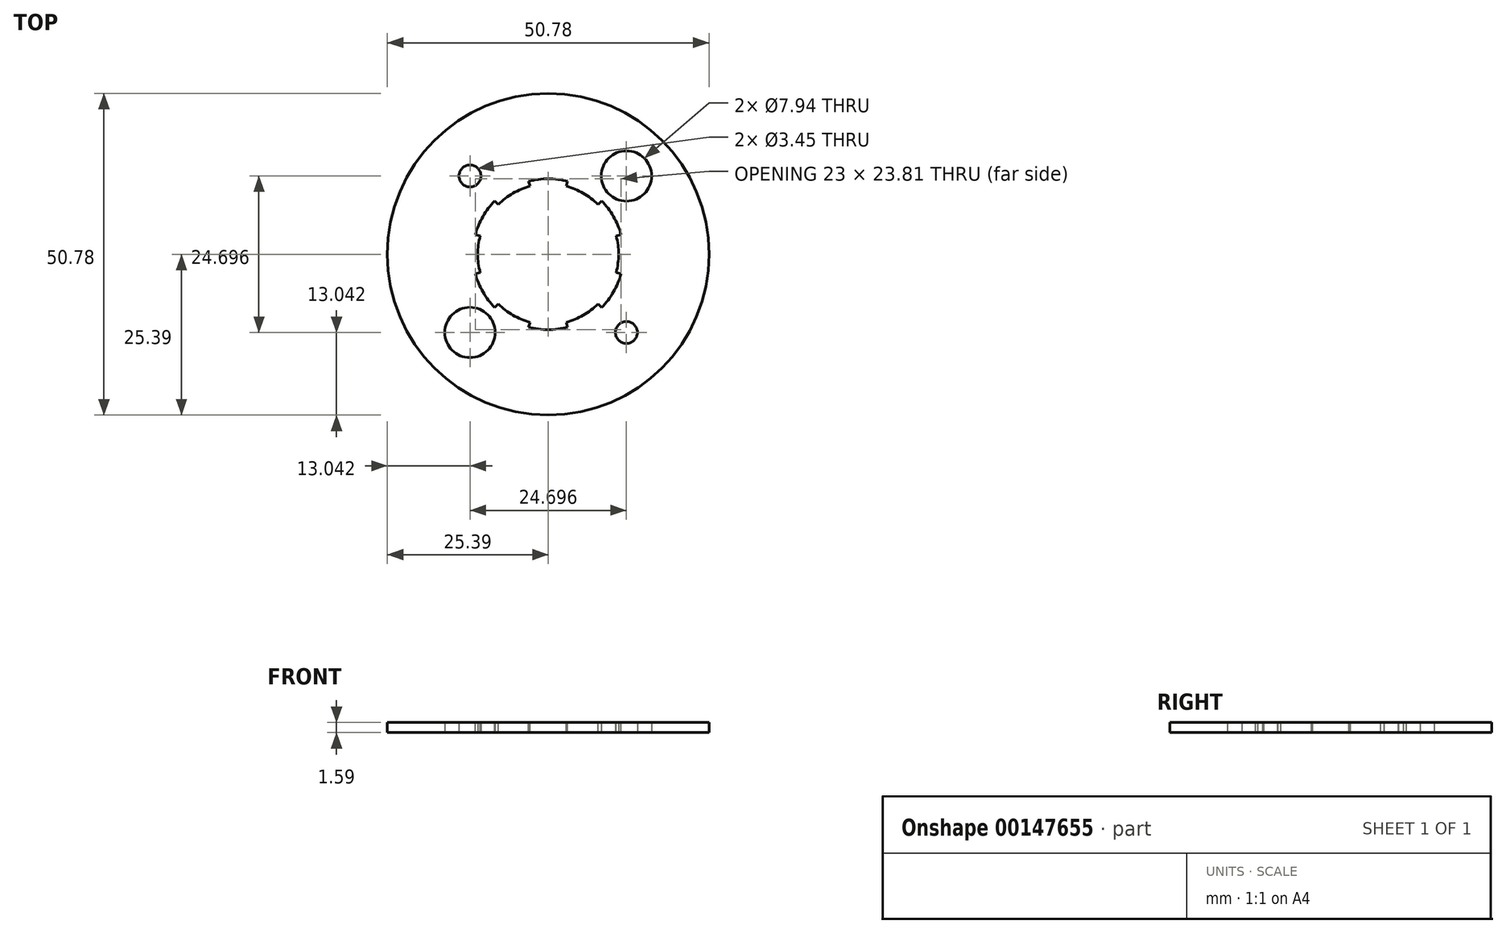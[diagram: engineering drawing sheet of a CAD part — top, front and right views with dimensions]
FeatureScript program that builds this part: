
annotation { "Feature Type Name" : "Feature", "Feature Type Description" : "" }
export const myFeature = defineFeature(function(context is Context, id is Id, definition is map)
    precondition{}
    {
        {
            var Q0;
            Q0=qCreatedBy(makeId("Top.planeOp"),FACE);
            var sketch = newSketch(context, id + "F0", { "sketchPlane" : qUnion([Q0])});
            skCircle(sketch, "E0", {"center": v(0, 0) * mm, "radius": 25.4 * mm});
            skCircle(sketch, "E1", {"center": v(0, 0) * mm, "radius": 11.11 * mm});
            skCircle(sketch, "E2", {"center": v(0, 0) * mm, "radius": 11.9 * mm, "construction": true});
            skLineSegment(sketch, "E3.bottom", {"start": v(-12.35, 12.35) * mm, "end": v(12.35, 12.35) * mm, "construction": true});
            skLineSegment(sketch, "E3.top", {"start": v(-12.35, -12.35) * mm, "end": v(12.35, -12.35) * mm, "construction": true});
            skLineSegment(sketch, "E3.left", {"start": v(-12.35, 12.35) * mm, "end": v(-12.35, -12.35) * mm, "construction": true});
            skLineSegment(sketch, "E3.right", {"start": v(12.35, 12.35) * mm, "end": v(12.35, -12.35) * mm, "construction": true});
            skCircle(sketch, "E4", {"center": v(-12.35, 12.35) * mm, "radius": 5.56 * mm, "construction": true});
            skCircle(sketch, "E5", {"center": v(12.35, 12.35) * mm, "radius": 3.97 * mm});
            skCircle(sketch, "E6", {"center": v(-12.35, 12.35) * mm, "radius": 1.73 * mm});
            skCircle(sketch, "E7", {"center": v(-12.35, -12.35) * mm, "radius": 3.97 * mm});
            skCircle(sketch, "E8", {"center": v(12.35, -12.35) * mm, "radius": 1.73 * mm});
            skSolve(sketch);
        }
        {
            var Q0;
            Q0=qSketchRegion(id+"F0",true);
            extrude(context, id + "F1", {"entities" : qUnion([Q0]), "depth" : 1.59 * mm});
        }
        {
            var Q0;
            Q0=makeQuery(id+"F1.opExtrude","CAP_FACE",FACE,{"disambiguationData":[OSD([sQuery(id+"F0.wireOp",EDGE,"E0"),sQuery(id+"F0.wireOp",EDGE,"E1")])],"isStart":false});
            var sketch = newSketch(context, id + "F2", { "sketchPlane" : qUnion([Q0])});
            skLineSegment(sketch, "E9", {"start": v(0, 0) * mm, "end": v(0, 11.11) * mm, "construction": true});
            skArc(sketch, "E10", {"start": v(2.88, 10.73) * mm, "mid": v(0, 11.11) * mm, "end": v(-2.88, 10.73) * mm});
            skLineSegment(sketch, "E11", {"start": v(-2.88, 10.73) * mm, "end": v(-3.08, 11.5) * mm});
            skLineSegment(sketch, "E12", {"start": v(2.88, 10.73) * mm, "end": v(3.08, 11.5) * mm});
            skLineSegment(sketch, "E13", {"start": v(0, 0) * mm, "end": v(-2.88, 10.73) * mm, "construction": true});
            skLineSegment(sketch, "E14", {"start": v(0, 0) * mm, "end": v(2.88, 10.73) * mm, "construction": true});
            skArc(sketch, "E15", {"start": v(3.08, 11.5) * mm, "mid": v(0, 11.9) * mm, "end": v(-3.08, 11.5) * mm});
            skSolve(sketch);
        }
        {
            var Q0;
            Q0=qSketchRegion(id+"F2",true);
            var Q1;
            Q1=makeQuery(id+"F1.opExtrude","CAP_FACE",FACE,{"disambiguationData":[OSD([sQuery(id+"F0.wireOp",EDGE,"E0"),sQuery(id+"F0.wireOp",EDGE,"E1")])],"isStart":true});
            extrude(context, id + "F3", {"entities" : qUnion([Q0]), "operationType" : NewBodyOperationType.REMOVE, "endBound" : BoundingType.UP_TO_SURFACE, "oppositeDirection" : true, "endBoundEntityFace" : qUnion([Q1]), "depth" : 25.4 * mm});
        }
        {
            var Q0;
            Q0=makeQuery(id+"F3.boolean.opBoolean","COPY",FACE,{"derivedFrom":makeQuery(id+"F3.opExtrude","SWEPT_FACE",FACE,{"disambiguationData":[OSD([sQuery(id+"F2.wireOp",EDGE,"E11")])]})});
            var Q1;
            Q1=makeQuery(id+"F3.boolean.opBoolean","COPY",FACE,{"derivedFrom":makeQuery(id+"F3.opExtrude","SWEPT_FACE",FACE,{"disambiguationData":[OSD([sQuery(id+"F2.wireOp",EDGE,"E15")])]})});
            var Q2;
            Q2=makeQuery(id+"F3.boolean.opBoolean","COPY",FACE,{"derivedFrom":makeQuery(id+"F3.opExtrude","SWEPT_FACE",FACE,{"disambiguationData":[OSD([sQuery(id+"F2.wireOp",EDGE,"E12")])]})});
            var Q3;
            Q3=makeQuery(id+"F1.opExtrude","SWEPT_FACE",FACE,{"disambiguationData":[OSD([sQuery(id+"F0.wireOp",EDGE,"E1")])]});
            circularPattern(context, id + "F4", {"patternType" : PatternType.FACE, "faces" : qUnion([Q0, Q1, Q2]), "axis" : qUnion([Q3]), "angle" : 60 * degree, "instanceCount" : 6});
        }
    });
